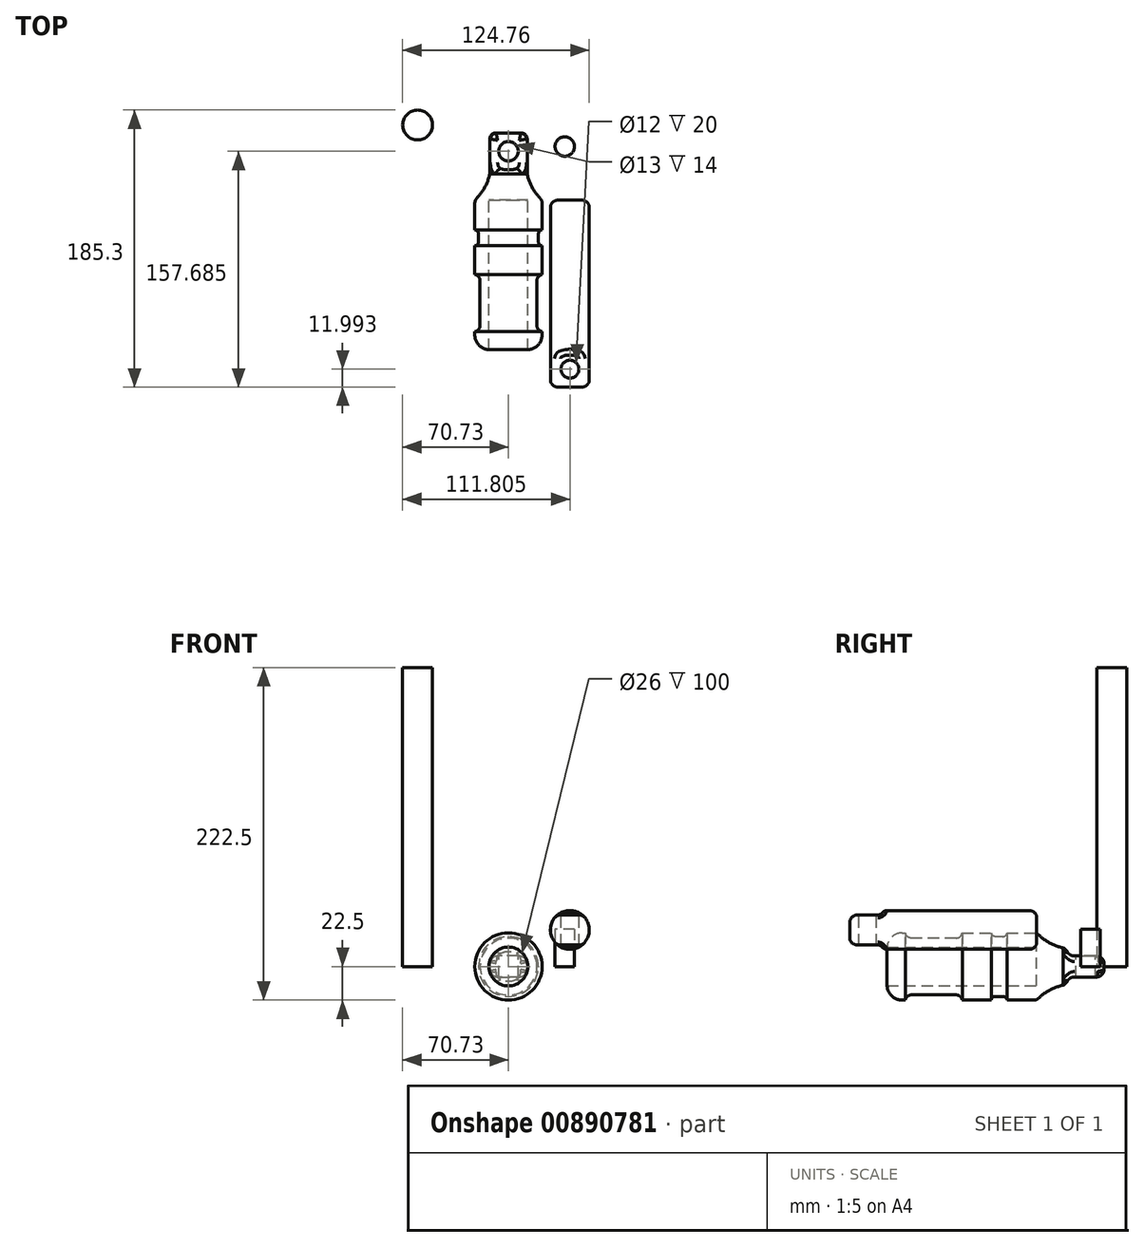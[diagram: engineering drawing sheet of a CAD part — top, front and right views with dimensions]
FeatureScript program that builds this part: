
annotation { "Feature Type Name" : "Feature", "Feature Type Description" : "" }
export const myFeature = defineFeature(function(context is Context, id is Id, definition is map)
    precondition{}
    {
        {
            var Q0;
            Q0=qCreatedBy(makeId("Front.planeOp"),FACE);
            var sketch = newSketch(context, id + "F0", { "sketchPlane" : qUnion([Q0])});
            skCircle(sketch, "E0", {"center": v(0, 0) * mm, "radius": 22.5 * mm});
            skCircle(sketch, "E1", {"center": v(0, 0) * mm, "radius": 13 * mm});
            skSolve(sketch);
        }
        {
            var Q0;
            Q0 = qSketchRegion(id + "F0", true);
            extrude(context, id + "F1", {"entities" : qUnion([Q0]), "depth" : 100 * mm, "offsetDistance" : 25 * mm});
        }
        {
            var Q0;
            Q0=qCreatedBy(makeId("Right.planeOp"),FACE);
            var sketch = newSketch(context, id + "F2", { "sketchPlane" : qUnion([Q0])});
            skLineSegment(sketch, "E2", {"start": v(0, 0) * mm, "end": v(0, -20.65) * mm});
            skLineSegment(sketch, "E3", {"start": v(45, 0) * mm, "end": v(45, 8.5) * mm});
            skLineSegment(sketch, "E4", {"start": v(41, 12.5) * mm, "end": v(17.61, 12.5) * mm});
            skLineSegment(sketch, "E5", {"start": v(0, 12.5) * mm, "end": v(0, 22.5) * mm});
            skArc(sketch, "E6", {"start": v(0, 22.5) * mm, "mid": v(8.04, 16.15) * mm, "end": v(17.61, 12.5) * mm});
            skLineSegment(sketch, "E7.MirrorCS", {"start": v(41, -12.5) * mm, "end": v(17.61, -12.5) * mm});
            skArc(sketch, "E8.MirrorCS", {"start": v(0, -22.5) * mm, "mid": v(8.04, -16.15) * mm, "end": v(17.61, -12.5) * mm});
            skLineSegment(sketch, "E9.MirrorCS", {"start": v(45, 0) * mm, "end": v(45, -8.5) * mm});
            skLineSegment(sketch, "E10", {"start": v(0, 12.5) * mm, "end": v(0, 0) * mm});
            skPoint(sketch, "E11.visualSharp", {"position": v(45, 12.5) * mm});
            skArc(sketch, "E11.filletArc", {"start": v(45, 8.5) * mm, "mid": v(43.83, 11.33) * mm, "end": v(41, 12.5) * mm});
            skPoint(sketch, "E12.visualSharp", {"position": v(45, -12.5) * mm});
            skArc(sketch, "E12.filletArc", {"start": v(41, -12.5) * mm, "mid": v(43.83, -11.33) * mm, "end": v(45, -8.5) * mm});
            skPoint(sketch, "E13.orphan", {"position": v(0, -12.5) * mm});
            skLineSegment(sketch, "E14", {"start": v(0, 22.5) * mm, "end": v(0, -22.5) * mm});
            skLineSegment(sketch, "E15", {"start": v(45, 0) * mm, "end": v(0, 0) * mm});
            skSolve(sketch);
        }
        {
            var Q0;
            Q0=makeQuery(id+"F2.imprint","IMPRINT",FACE,{"disambiguationData":[TD([[makeQuery(id+"F2.imprint","IMPRINT",EDGE,{"derivedFrom":sQuery(id+"F2.wireOp",EDGE,"E3")}),1.0]])]});
            var Q1;
            Q1=sQuery(id+"F2.wireOp",EDGE,"E15");
            revolve(context, id + "F3", {"operationType" : NewBodyOperationType.ADD, "surfaceOperationType" : NewSurfaceOperationType.NEW, "entities" : qUnion([Q0]), "axis" : qUnion([Q1]), "revolveType" : RevolveType.FULL});
        }
        {
            var Q0;
            Q0=qCreatedBy(makeId("Right.planeOp"),FACE);
            var sketch = newSketch(context, id + "F4", { "sketchPlane" : qUnion([Q0])});
            skLineSegment(sketch, "E16", {"start": v(0, 0) * mm, "end": v(45.5, 0) * mm});
            skLineSegment(sketch, "E17", {"start": v(45.5, 0) * mm, "end": v(45.5, 7) * mm});
            skLineSegment(sketch, "E18", {"start": v(45.5, 7) * mm, "end": v(25.32, 7) * mm});
            skArc(sketch, "E19", {"start": v(19.7, 12.63) * mm, "mid": v(21.34, 8.65) * mm, "end": v(25.32, 7) * mm});
            skLineSegment(sketch, "E20", {"start": v(19.7, 12.63) * mm, "end": v(19.7, 21.17) * mm});
            skLineSegment(sketch, "E21", {"start": v(19.7, 21.17) * mm, "end": v(45.5, 21.17) * mm});
            skLineSegment(sketch, "E22", {"start": v(45.5, 21.17) * mm, "end": v(45.5, 7) * mm});
            skLineSegment(sketch, "E23.MirrorCS", {"start": v(45.5, -7) * mm, "end": v(25.32, -7) * mm});
            skLineSegment(sketch, "E24.MirrorCS", {"start": v(45.5, -21.17) * mm, "end": v(45.5, -7) * mm});
            skLineSegment(sketch, "E25.MirrorCS", {"start": v(19.7, -21.17) * mm, "end": v(45.5, -21.17) * mm});
            skLineSegment(sketch, "E26.MirrorCS", {"start": v(19.7, -12.63) * mm, "end": v(19.7, -21.17) * mm});
            skArc(sketch, "E27.MirrorCS", {"start": v(19.7, -12.63) * mm, "mid": v(21.34, -8.65) * mm, "end": v(25.32, -7) * mm});
            skSolve(sketch);
        }
        {
            var Q0;
            Q0=makeQuery(id+"F4.imprint","IMPRINT",FACE,{"disambiguationData":[TD([[makeQuery(id+"F4.imprint","IMPRINT",EDGE,{"derivedFrom":sQuery(id+"F4.wireOp",EDGE,"E18")}),-1.0]])]});
            var Q1;
            Q1=makeQuery(id+"F4.imprint","IMPRINT",FACE,{"disambiguationData":[TD([[makeQuery(id+"F4.imprint","IMPRINT",EDGE,{"derivedFrom":sQuery(id+"F4.wireOp",EDGE,"E23.MirrorCS")}),1.0]])]});
            extrude(context, id + "F5", {"entities" : qUnion([Q0, Q1]), "operationType" : NewBodyOperationType.REMOVE, "endBound" : BoundingType.SYMMETRIC, "depth" : 25 * mm, "offsetDistance" : 25 * mm});
        }
        {
            var Q0;
            Q0=makeQuery(id+"F5.boolean.opBoolean","INTERSECT",EDGE,{"derivedFrom":[makeQuery(id+"F3.opRevolve","SWEPT_FACE",FACE,{"disambiguationData":[OSD([sQuery(id+"F2.wireOp",EDGE,"E3")])]}),makeQuery(id+"F5.opExtrude","SWEPT_FACE",FACE,{"disambiguationData":[OSD([sQuery(id+"F4.wireOp",EDGE,"E18")])]})]});
            var Q1;
            Q1=makeQuery(id+"F5.boolean.opBoolean","INTERSECT",EDGE,{"derivedFrom":[makeQuery(id+"F3.opRevolve","SWEPT_FACE",FACE,{"disambiguationData":[OSD([sQuery(id+"F2.wireOp",EDGE,"E3")])]}),makeQuery(id+"F5.opExtrude","SWEPT_FACE",FACE,{"disambiguationData":[OSD([sQuery(id+"F4.wireOp",EDGE,"E23.MirrorCS")])]})]});
            fillet(context, id + "F6", {"entities" : qUnion([Q0, Q1]), "radius" : 5 * mm, "tangentPropagation" : true, "allowEdgeOverflow" : false});
        }
        {
            var Q0;
            Q0=makeQuery(id+"F5.boolean.opBoolean","COPY",FACE,{"derivedFrom":makeQuery(id+"F5.opExtrude","SWEPT_FACE",FACE,{"disambiguationData":[OSD([sQuery(id+"F4.wireOp",EDGE,"E18")])]})});
            var sketch = newSketch(context, id + "F7", { "sketchPlane" : qUnion([Q0])});
            skCircle(sketch, "E28", {"center": v(0, 32.69) * mm, "radius": 6.5 * mm});
            skPoint(sketch, "E29", {"position": v(0, 40) * mm});
            skSolve(sketch);
        }
        {
            var Q0;
            Q0=makeQuery(id+"F7.imprint","IMPRINT",FACE,{"disambiguationData":[TD([[makeQuery(id+"F7.imprint","IMPRINT",EDGE,{"derivedFrom":sQuery(id+"F7.wireOp",EDGE,"E28")}),1.0]])]});
            extrude(context, id + "F8", {"entities" : qUnion([Q0]), "operationType" : NewBodyOperationType.REMOVE, "oppositeDirection" : true, "depth" : 25 * mm, "offsetDistance" : 25 * mm});
        }
        {
            var Q0;
            Q0=makeQuery(id+"F1.opExtrude","CAP_EDGE",EDGE,{"disambiguationData":[OSD([sQuery(id+"F0.wireOp",EDGE,"E0")])],"isStart":false});
            fillet(context, id + "F9", {"entities" : qUnion([Q0]), "radius" : 10 * mm, "tangentPropagation" : true, "allowEdgeOverflow" : false});
        }
        {
            var Q0;
            Q0=makeQuery(id+"F3.boolean.opBoolean","MERGE",EDGE,{"derivedFrom":[makeQuery(id+"F1.opExtrude","CAP_EDGE",EDGE,{"disambiguationData":[OSD([sQuery(id+"F0.wireOp",EDGE,"E0")])],"isStart":true}),makeQuery(id+"F3.opRevolve","SWEPT_EDGE",EDGE,{"disambiguationData":[OSD([sQuery(id+"F2.wireOp",EDGE,"E6"),sQuery(id+"F2.wireOp",EDGE,"E14")])]})]});
            fillet(context, id + "F10", {"entities" : qUnion([Q0]), "radius" : 5 * mm, "tangentPropagation" : true, "allowEdgeOverflow" : false});
        }
        {
            var Q0;
            Q0=qCreatedBy(makeId("Right.planeOp"),FACE);
            var sketch = newSketch(context, id + "F11", { "sketchPlane" : qUnion([Q0])});
            skLineSegment(sketch, "E30", {"start": v(0, 0) * mm, "end": v(-81.06, 0) * mm});
            skLineSegment(sketch, "E31", {"start": v(-68.82, 0) * mm, "end": v(-68.82, 19) * mm});
            skLineSegment(sketch, "E32", {"start": v(-68.82, 19) * mm, "end": v(-53.82, 19) * mm});
            skArc(sketch, "E33", {"start": v(-53.82, 19) * mm, "mid": v(-50.96, 20.17) * mm, "end": v(-49.74, 23) * mm});
            skLineSegment(sketch, "E34", {"start": v(-49.74, 23) * mm, "end": v(-71.93, 23) * mm});
            skLineSegment(sketch, "E35.MirrorCS", {"start": v(-68.82, 19) * mm, "end": v(-83.82, 19) * mm});
            skLineSegment(sketch, "E36.MirrorCS", {"start": v(-87.89, 23) * mm, "end": v(-65.7, 23) * mm});
            skArc(sketch, "E37.MirrorCS", {"start": v(-83.82, 19) * mm, "mid": v(-86.67, 20.17) * mm, "end": v(-87.89, 23) * mm});
            skLineSegment(sketch, "E38", {"start": v(-25.17, 0) * mm, "end": v(-25.17, 20) * mm});
            skLineSegment(sketch, "E39", {"start": v(-25.17, 20) * mm, "end": v(-22.67, 20) * mm});
            skArc(sketch, "E40", {"start": v(-22.67, 20) * mm, "mid": v(-20.75, 20.75) * mm, "end": v(-19.86, 22.6) * mm});
            skLineSegment(sketch, "E41.MirrorCS", {"start": v(-25.17, 20) * mm, "end": v(-27.67, 20) * mm});
            skArc(sketch, "E42.MirrorCS", {"start": v(-27.67, 20) * mm, "mid": v(-29.58, 20.75) * mm, "end": v(-30.48, 22.6) * mm});
            skLineSegment(sketch, "E43", {"start": v(-30.48, 22.6) * mm, "end": v(-19.86, 22.6) * mm});
            skLineSegment(sketch, "E44", {"start": v(-19.86, 22.6) * mm, "end": v(-17.86, 22.6) * mm});
            skLineSegment(sketch, "E45", {"start": v(-17.86, 22.6) * mm, "end": v(-17.86, 11.62) * mm});
            skLineSegment(sketch, "E46.MirrorCS", {"start": v(-30.48, 22.6) * mm, "end": v(-32.48, 22.6) * mm});
            skLineSegment(sketch, "E47.MirrorCS", {"start": v(-32.48, 22.6) * mm, "end": v(-32.48, 11.62) * mm});
            skArc(sketch, "E48.MirrorCS", {"start": v(-37.29, 20) * mm, "mid": v(-35.37, 20.75) * mm, "end": v(-34.48, 22.6) * mm});
            skArc(sketch, "E49.MirrorCS", {"start": v(-42.29, 20) * mm, "mid": v(-44.2, 20.75) * mm, "end": v(-45.1, 22.6) * mm});
            skLineSegment(sketch, "E50.MirrorCS", {"start": v(-34.48, 22.6) * mm, "end": v(-45.1, 22.6) * mm});
            skLineSegment(sketch, "E51.MirrorCS", {"start": v(-39.79, 20) * mm, "end": v(-37.29, 20) * mm});
            skLineSegment(sketch, "E52.MirrorCS", {"start": v(-39.79, 20) * mm, "end": v(-42.29, 20) * mm});
            skArc(sketch, "E53.MirrorCS", {"start": v(-13.05, 20) * mm, "mid": v(-14.96, 20.75) * mm, "end": v(-15.86, 22.6) * mm});
            skLineSegment(sketch, "E54.MirrorCS", {"start": v(-5.24, 22.6) * mm, "end": v(-15.86, 22.6) * mm});
            skArc(sketch, "E55.MirrorCS", {"start": v(-8.05, 20) * mm, "mid": v(-6.13, 20.75) * mm, "end": v(-5.24, 22.6) * mm});
            skLineSegment(sketch, "E56.MirrorCS", {"start": v(-10.55, 20) * mm, "end": v(-8.05, 20) * mm});
            skLineSegment(sketch, "E57.MirrorCS", {"start": v(-10.55, 20) * mm, "end": v(-13.05, 20) * mm});
            skSolve(sketch);
        }
        {
            var Q0;
            Q0=makeQuery(id+"F11.imprint","IMPRINT",FACE,{"disambiguationData":[TD([[makeQuery(id+"F11.imprint","IMPRINT",EDGE,{"derivedFrom":sQuery(id+"F11.wireOp",EDGE,"E32")}),1.0]])]});
            var Q1;
            Q1=makeQuery(id+"F11.imprint","IMPRINT",FACE,{"disambiguationData":[TD([[makeQuery(id+"F11.imprint","IMPRINT",EDGE,{"derivedFrom":sQuery(id+"F11.wireOp",EDGE,"E39")}),1.0]])]});
            var Q2;
            Q2=makeQuery(id+"F11.imprint","IMPRINT",FACE,{"disambiguationData":[TD([[makeQuery(id+"F11.imprint","IMPRINT",EDGE,{"derivedFrom":sQuery(id+"F11.wireOp",EDGE,"E53.MirrorCS")}),-1.0]])]});
            var Q3;
            Q3=sQuery(id+"F11.wireOp",EDGE,"E30");
            revolve(context, id + "F12", {"operationType" : NewBodyOperationType.REMOVE, "surfaceOperationType" : NewSurfaceOperationType.NEW, "entities" : qUnion([Q0, Q1, Q2]), "axis" : qUnion([Q3]), "revolveType" : RevolveType.FULL, "oppositeDirection" : true});
        }
        {
            var Q0;
            Q0=qCreatedBy(makeId("Front.planeOp"),FACE);
            var sketch = newSketch(context, id + "F13", { "sketchPlane" : qUnion([Q0])});
            skCircle(sketch, "E58", {"center": v(41.03, 24.44) * mm, "radius": 13 * mm});
            skSolve(sketch);
        }
        {
            var Q0;
            Q0=makeQuery(id+"F13.imprint","IMPRINT",FACE,{"disambiguationData":[TD([[makeQuery(id+"F13.imprint","IMPRINT",EDGE,{"derivedFrom":sQuery(id+"F13.wireOp",EDGE,"E58")}),1.0]])]});
            extrude(context, id + "F14", {"entities" : qUnion([Q0]), "depth" : 125 * mm, "offsetDistance" : 25 * mm});
        }
        {
            var Q0;
            Q0=qCreatedBy(makeId("Top.planeOp"),FACE);
            var sketch = newSketch(context, id + "F15", { "sketchPlane" : qUnion([Q0])});
            skLineSegment(sketch, "E59", {"start": v(41.07, 0) * mm, "end": v(41.07, -106.01) * mm});
            skLineSegment(sketch, "E60", {"start": v(41.07, -106.01) * mm, "end": v(51.07, -106.01) * mm});
            skLineSegment(sketch, "E61", {"start": v(51.07, -106.01) * mm, "end": v(51.07, -135.96) * mm});
            skLineSegment(sketch, "E62", {"start": v(41.07, 0) * mm, "end": v(54.07, 0) * mm});
            skLineSegment(sketch, "E63", {"start": v(41.07, 0) * mm, "end": v(28.07, 0) * mm});
            skArc(sketch, "E64", {"start": v(54.32, -102.97) * mm, "mid": v(52.04, -103.79) * mm, "end": v(51.07, -106.01) * mm});
            skLineSegment(sketch, "E65", {"start": v(54.32, -102.97) * mm, "end": v(59.68, -102.97) * mm});
            skLineSegment(sketch, "E66", {"start": v(59.68, -102.97) * mm, "end": v(59.68, -135.96) * mm});
            skLineSegment(sketch, "E67", {"start": v(59.68, -135.96) * mm, "end": v(51.07, -135.96) * mm});
            skArc(sketch, "E68.MirrorCS", {"start": v(27.82, -102.97) * mm, "mid": v(30.1, -103.79) * mm, "end": v(31.07, -106.01) * mm});
            skLineSegment(sketch, "E69.MirrorCS", {"start": v(27.82, -102.97) * mm, "end": v(22.47, -102.97) * mm});
            skLineSegment(sketch, "E70.MirrorCS", {"start": v(22.47, -102.97) * mm, "end": v(22.47, -135.96) * mm});
            skLineSegment(sketch, "E71.MirrorCS", {"start": v(31.07, -106.01) * mm, "end": v(31.07, -135.96) * mm});
            skLineSegment(sketch, "E72.MirrorCS", {"start": v(22.47, -135.96) * mm, "end": v(31.07, -135.96) * mm});
            skSolve(sketch);
        }
        {
            var Q0;
            Q0 = qSketchRegion(id + "F15", true);
            extrude(context, id + "F16", {"entities" : qUnion([Q0]), "operationType" : NewBodyOperationType.REMOVE, "depth" : 37.2 * mm, "offsetDistance" : 25 * mm});
        }
        {
            var Q0;
            Q0=makeQuery(id+"F14.opExtrude","CAP_FACE",FACE,{"disambiguationData":[OSD([sQuery(id+"F13.wireOp",EDGE,"E58")])],"isStart":false});
            var Q1;
            Q1=makeQuery(id+"F16.boolean.opBoolean","INTERSECT",EDGE,{"disambiguationData":[OD(1.0)],"derivedFrom":[makeQuery(id+"F14.opExtrude","SWEPT_FACE",FACE,{"disambiguationData":[OSD([sQuery(id+"F13.wireOp",EDGE,"E58")])]}),makeQuery(id+"F16.opExtrude","SWEPT_FACE",FACE,{"disambiguationData":[OSD([sQuery(id+"F15.wireOp",EDGE,"E71.MirrorCS")])]})]});
            var Q2;
            Q2=makeQuery(id+"F16.boolean.opBoolean","INTERSECT",EDGE,{"derivedFrom":[makeQuery(id+"F14.opExtrude","SWEPT_FACE",FACE,{"disambiguationData":[OSD([sQuery(id+"F13.wireOp",EDGE,"E58")])]}),makeQuery(id+"F16.opExtrude","SWEPT_FACE",FACE,{"disambiguationData":[OSD([sQuery(id+"F15.wireOp",EDGE,"E64")])]})]});
            var Q3;
            Q3=makeQuery(id+"F16.boolean.opBoolean","INTERSECT",EDGE,{"disambiguationData":[OD(1.0)],"derivedFrom":[makeQuery(id+"F14.opExtrude","SWEPT_FACE",FACE,{"disambiguationData":[OSD([sQuery(id+"F13.wireOp",EDGE,"E58")])]}),makeQuery(id+"F16.opExtrude","SWEPT_FACE",FACE,{"disambiguationData":[OSD([sQuery(id+"F15.wireOp",EDGE,"E61")])]})]});
            var Q4;
            Q4=makeQuery(id+"F16.boolean.opBoolean","INTERSECT",EDGE,{"disambiguationData":[OD(0.0)],"derivedFrom":[makeQuery(id+"F14.opExtrude","SWEPT_FACE",FACE,{"disambiguationData":[OSD([sQuery(id+"F13.wireOp",EDGE,"E58")])]}),makeQuery(id+"F16.opExtrude","SWEPT_FACE",FACE,{"disambiguationData":[OSD([sQuery(id+"F15.wireOp",EDGE,"E61")])]})]});
            var Q5;
            Q5=makeQuery(id+"F14.opExtrude","CAP_EDGE",EDGE,{"disambiguationData":[OSD([sQuery(id+"F13.wireOp",EDGE,"E58")])],"isStart":true});
            var Q6;
            Q6=makeQuery(id+"F16.boolean.opBoolean","INTERSECT",EDGE,{"derivedFrom":[makeQuery(id+"F14.opExtrude","SWEPT_FACE",FACE,{"disambiguationData":[OSD([sQuery(id+"F13.wireOp",EDGE,"E58")])]}),makeQuery(id+"F16.opExtrude","SWEPT_FACE",FACE,{"disambiguationData":[OSD([sQuery(id+"F15.wireOp",EDGE,"E68.MirrorCS")])]})]});
            var Q7;
            Q7=makeQuery(id+"F16.boolean.opBoolean","COPY",FACE,{"derivedFrom":makeQuery(id+"F16.opExtrude","SWEPT_FACE",FACE,{"disambiguationData":[OSD([sQuery(id+"F15.wireOp",EDGE,"E71.MirrorCS")])]})});
            fillet(context, id + "F17", {"entities" : qUnion([Q0, Q1, Q2, Q3, Q4, Q5, Q6, Q7]), "radius" : 5 * mm, "tangentPropagation" : true, "allowEdgeOverflow" : false});
        }
        {
            var Q0;
            Q0=makeQuery(id+"F16.boolean.opBoolean","COPY",FACE,{"derivedFrom":makeQuery(id+"F16.opExtrude","SWEPT_FACE",FACE,{"disambiguationData":[OSD([sQuery(id+"F15.wireOp",EDGE,"E71.MirrorCS")])]})});
            var sketch = newSketch(context, id + "F18", { "sketchPlane" : qUnion([Q0])});
            skCircle(sketch, "E73", {"center": v(113, 24.48) * mm, "radius": 6 * mm});
            skPoint(sketch, "E73.centerSnap0", {"position": v(113, 30.72) * mm});
            skSolve(sketch);
        }
        {
            var Q0;
            Q0 = qSketchRegion(id + "F18", true);
            extrude(context, id + "F19", {"entities" : qUnion([Q0]), "operationType" : NewBodyOperationType.REMOVE, "oppositeDirection" : true, "depth" : 25 * mm, "offsetDistance" : 25 * mm});
        }
        {
            var Q0;
            Q0=makeQuery(id+"F14.opExtrude","SWEPT_BODY",BODY,{"disambiguationData":[OSD([sQuery(id+"F13.wireOp",EDGE,"E58")])]});
            var Q1;
            Q1=makeQuery(id+"F14.opExtrude","SWEPT_FACE",FACE,{"disambiguationData":[OSD([sQuery(id+"F13.wireOp",EDGE,"E58")])]});
            transform(context, id + "F20", {"entities" : qUnion([Q0]), "transformType" : TransformType.ROTATION, "transformAxis" : qUnion([Q1]), "angle" : 90 * degree, "makeCopy" : false});
        }
        {
            var Q0;
            Q0=qCreatedBy(makeId("Top.planeOp"),FACE);
            var sketch = newSketch(context, id + "F21", { "sketchPlane" : qUnion([Q0])});
            skCircle(sketch, "E74", {"center": v(37.62, 35.88) * mm, "radius": 6.5 * mm});
            skSolve(sketch);
        }
        {
            var Q0;
            Q0 = qSketchRegion(id + "F21", true);
            extrude(context, id + "F22", {"entities" : qUnion([Q0]), "depth" : 25 * mm, "offsetDistance" : 25 * mm});
        }
        {
            var Q0;
            Q0=qCreatedBy(makeId("Top.planeOp"),FACE);
            var sketch = newSketch(context, id + "F23", { "sketchPlane" : qUnion([Q0])});
            skCircle(sketch, "E75", {"center": v(-60.73, 50.3) * mm, "radius": 10 * mm});
            skSolve(sketch);
        }
        {
            var Q0;
            Q0=makeQuery(id+"F23.imprint","IMPRINT",FACE,{"disambiguationData":[TD([[makeQuery(id+"F23.imprint","IMPRINT",EDGE,{"derivedFrom":sQuery(id+"F23.wireOp",EDGE,"E75")}),1.0]])]});
            extrude(context, id + "F24", {"entities" : qUnion([Q0]), "depth" : 200 * mm, "offsetDistance" : 25 * mm});
        }
    });
